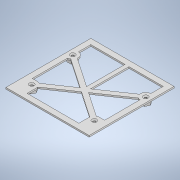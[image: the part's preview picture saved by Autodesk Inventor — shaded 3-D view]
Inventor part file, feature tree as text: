
AUTODESK INVENTOR PART (.ipt)
format: ipt  version: 2020.2 (Build 242310000, 310)  size: 285,696 bytes
history: native  units: mm
features: projected_geometry x5, sketch x4, extrude x3, hole x1
ambient origin geometry x8: Origin, YZ Plane, XZ Plane, XY Plane, X Axis, Y Axis, Z Axis, Center Point
bodies: Solid1 (feature_tree)
feature tree (13):
  extrude  "Extrusion1"  Depth=2.0mm
  extrude  "Extrusion2"  Depth=2.0mm
  hole  "Hole1"  [1 undecoded]
  extrude  "Extrusion3"  Depth=7.0mm
  sketch  "Sketch1"  dims[d0=160.0mm d1=2.0mm]
  sketch  "Sketch2"  dims[d2=2.0mm d3=0.0mm d4=5.5mm]
  sketch  "Sketch3"  dims[d5=5.5mm d6=5.5mm]
  projected_geometry  "Projected Loop1"
  projected_geometry  "Projected Loop2"
  projected_geometry  "Projected Loop3"
  projected_geometry  "Projected Loop4"
  sketch  "Sketch4"  dims[d7=5.5mm d8=81.28mm d9=94.742mm d10=24.999mm d11=35.001mm d12=0.1mm d13=0.1mm d14=0.1mm d15=0.1mm d16=2.0mm d17=2.0mm d18=2.0mm d19=2.0mm d20=5.0mm d21=0.0mm d22=3.4mm d23=6.0mm d24=6.3mm d25=2.0mm d26=90.0deg d27=8.0mm d28=20.594885mm d35=7.0mm d39=7.0mm d43=3.0mm d44=3.0mm d45=3.0mm d46=3.0mm d47=5.0mm d48=0.0mm d49=0.0mm d50=14.0mm d51=14.0mm d52=14.0mm d53=14.0mm d54=7.0mm]
  projected_geometry  "Projected Loop5"
note: 1 required parameter value undecoded (feature->parameter linkage not recoverable at this tier; creation-order binding heuristic only, values carry confidence <= 0.55)
